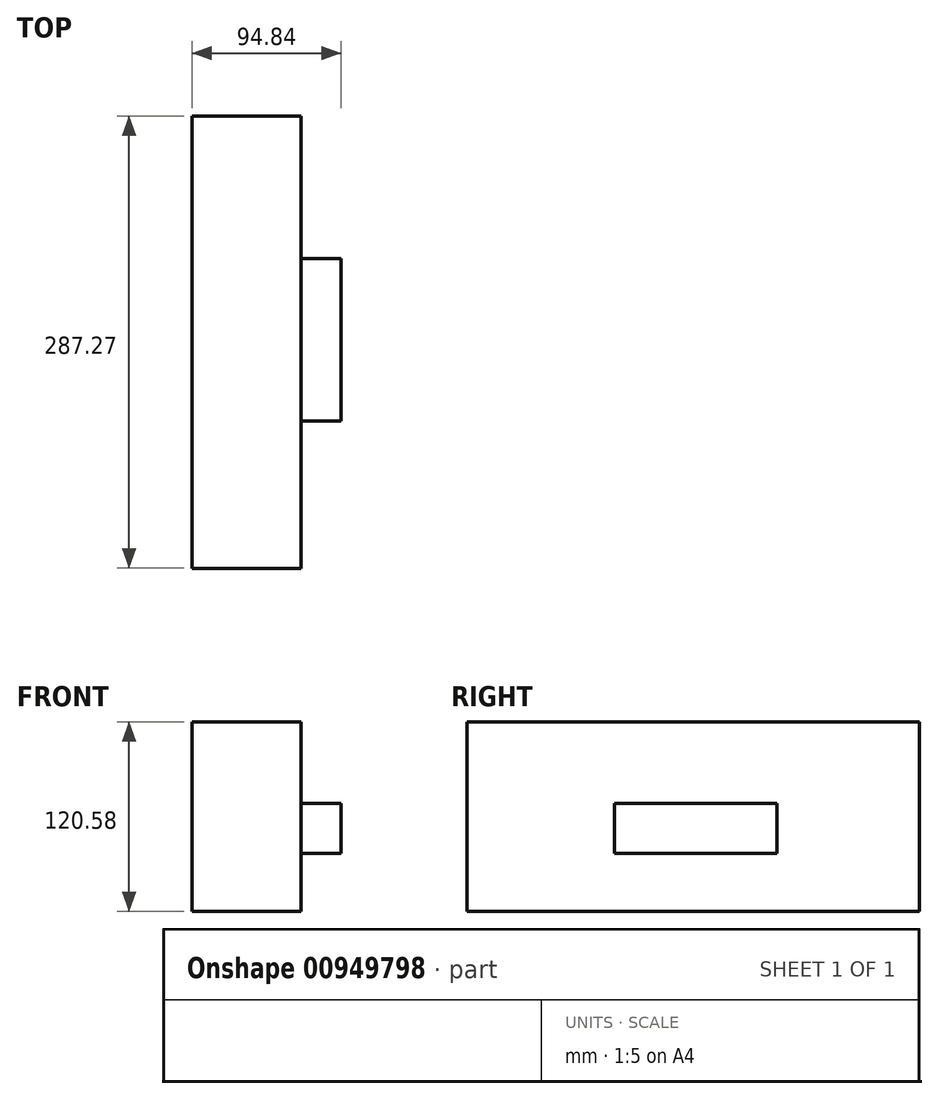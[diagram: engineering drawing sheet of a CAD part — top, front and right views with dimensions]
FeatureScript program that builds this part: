
annotation { "Feature Type Name" : "Feature", "Feature Type Description" : "" }
export const myFeature = defineFeature(function(context is Context, id is Id, definition is map)
    precondition{}
    {
        {
            var Q0;
            Q0=qCreatedBy(makeId("Front.planeOp"),FACE);
            var sketch = newSketch(context, id + "F0", { "sketchPlane" : qUnion([Q0])});
            skLineSegment(sketch, "E0.bottom", {"start": v(0, 0) * mm, "end": v(69.44, 0) * mm});
            skLineSegment(sketch, "E0.top", {"start": v(0, 40.57) * mm, "end": v(69.44, 40.57) * mm});
            skLineSegment(sketch, "E0.left", {"start": v(0, 0) * mm, "end": v(0, 40.57) * mm});
            skLineSegment(sketch, "E0.right", {"start": v(69.44, 0) * mm, "end": v(69.44, 40.57) * mm});
            skSolve(sketch);
        }
        {
            var Q0;
            Q0 = qSketchRegion(id + "F0", true);
            extrude(context, id + "F1", {"entities" : qUnion([Q0]), "depth" : 181.86 * mm, "offsetDistance" : 25.4 * mm});
        }
        {
            var Q0;
            Q0 = qConstructionFilter(qBodyType(qCreatedBy(id + "F0" ,EDGE), BodyType.WIRE), ConstructionObject.NO);
            extrude(context, id + "F2", {"bodyType" : ToolBodyType.SURFACE, "surfaceEntities" : qUnion([Q0]), "oppositeDirection" : true, "depth" : 64 * mm, "offsetDistance" : 25.4 * mm});
        }
        {
            var Q0;
            Q0=makeQuery(id+"F1.opExtrude","SWEPT_FACE",FACE,{"disambiguationData":[OSD([sQuery(id+"F0.wireOp",EDGE,"E0.top")])]});
            extrude(context, id + "F3", {"entities" : qUnion([Q0]), "operationType" : NewBodyOperationType.ADD, "depth" : 80 * mm, "offsetDistance" : 25.4 * mm});
        }
        {
            var Q0;
            {var subQ0=sQuery(id+"F0.wireOp",EDGE,"E0.top");Q0=makeQuery(id+"F3.boolean.opBoolean","MERGE",FACE,{"derivedFrom":[makeQuery(id+"F1.opExtrude","CAP_FACE",FACE,{"disambiguationData":[OSD([sQuery(id+"F0.wireOp",EDGE,"E0.bottom"),subQ0,sQuery(id+"F0.wireOp",EDGE,"E0.left"),sQuery(id+"F0.wireOp",EDGE,"E0.right")])],"isStart":false}),makeQuery(id+"F3.opExtrude","SWEPT_FACE",FACE,{"disambiguationData":[OSD([subQ0]),TDD([makeQuery(id+"F1.opExtrude","CAP_EDGE",EDGE,{"disambiguationData":[OSD([subQ0])],"isStart":false})])]})]});}
            extrude(context, id + "F4", {"entities" : qUnion([Q0]), "operationType" : NewBodyOperationType.ADD, "depth" : 105.4 * mm, "offsetDistance" : 25.4 * mm});
        }
        {
            var Q0;
            {var subQ0=sQuery(id+"F0.wireOp",EDGE,"E0.right");var subQ1=sQuery(id+"F0.wireOp",EDGE,"E0.top");Q0=makeQuery(id+"F4.boolean.opBoolean","MERGE",FACE,{"derivedFrom":[makeQuery(id+"F3.boolean.opBoolean","MERGE",FACE,{"derivedFrom":[makeQuery(id+"F1.opExtrude","SWEPT_FACE",FACE,{"disambiguationData":[OSD([subQ0])]}),makeQuery(id+"F3.opExtrude","SWEPT_FACE",FACE,{"disambiguationData":[OSD([subQ1,subQ0])]})]}),makeQuery(id+"F4.opExtrude","SWEPT_FACE",FACE,{"disambiguationData":[OSD([subQ1,subQ0])]})]});}
            var sketch = newSketch(context, id + "F5", { "sketchPlane" : qUnion([Q0])});
            skLineSegment(sketch, "E1.bottom", {"start": v(-193.8, 68.63) * mm, "end": v(-90.7, 68.63) * mm});
            skLineSegment(sketch, "E1.top", {"start": v(-193.8, 36.9) * mm, "end": v(-90.7, 36.9) * mm});
            skLineSegment(sketch, "E1.left", {"start": v(-193.8, 68.63) * mm, "end": v(-193.8, 36.9) * mm});
            skLineSegment(sketch, "E1.right", {"start": v(-90.7, 68.63) * mm, "end": v(-90.7, 36.9) * mm});
            skSolve(sketch);
        }
        {
            var Q0;
            Q0 = qSketchRegion(id + "F5", true);
            extrude(context, id + "F6", {"entities" : qUnion([Q0]), "operationType" : NewBodyOperationType.ADD, "depth" : 25.4 * mm, "offsetDistance" : 25.4 * mm});
        }
    });
